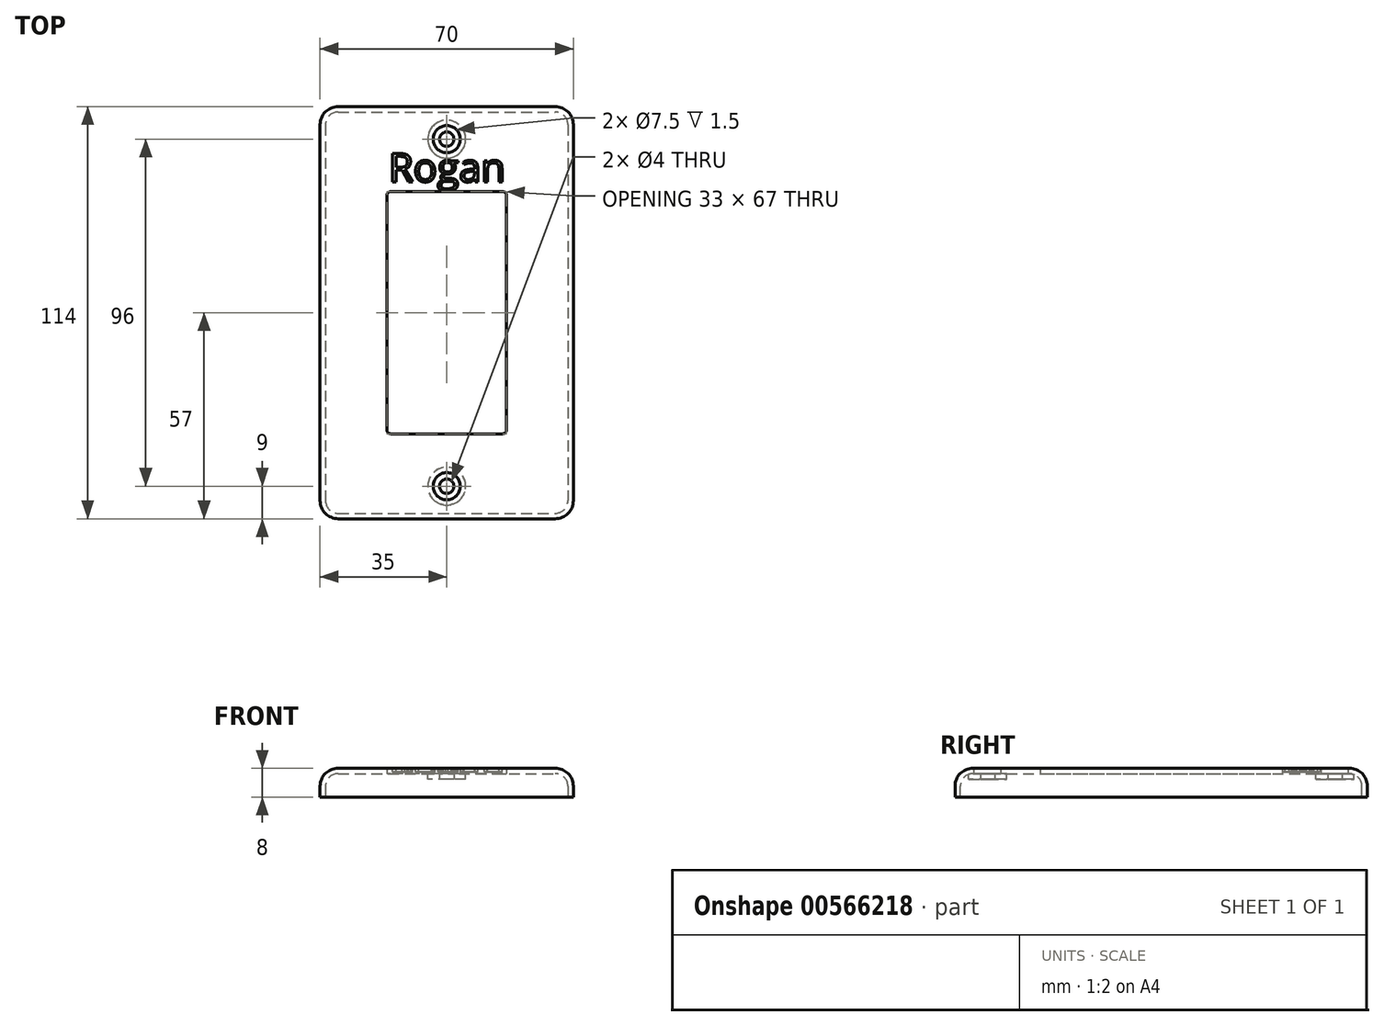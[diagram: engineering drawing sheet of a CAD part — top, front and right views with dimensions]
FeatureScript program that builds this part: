
annotation { "Feature Type Name" : "Feature", "Feature Type Description" : "" }
export const myFeature = defineFeature(function(context is Context, id is Id, definition is map)
    precondition{}
    {
        {
            var Q0;
            Q0=qCreatedBy(makeId("Top.planeOp"),FACE);
            var sketch = newSketch(context, id + "F0", { "sketchPlane" : qUnion([Q0])});
            skLineSegment(sketch, "E0.bottom", {"start": v(-35, 57) * mm, "end": v(35, 57) * mm});
            skLineSegment(sketch, "E0.top", {"start": v(-35, -57) * mm, "end": v(35, -57) * mm});
            skLineSegment(sketch, "E0.left", {"start": v(-35, 57) * mm, "end": v(-35, -57) * mm});
            skLineSegment(sketch, "E0.right", {"start": v(35, 57) * mm, "end": v(35, -57) * mm});
            skLineSegment(sketch, "E1.bottom", {"start": v(-16.5, 33.5) * mm, "end": v(16.5, 33.5) * mm});
            skLineSegment(sketch, "E1.top", {"start": v(-16.5, -33.5) * mm, "end": v(16.5, -33.5) * mm});
            skLineSegment(sketch, "E1.left", {"start": v(-16.5, 33.5) * mm, "end": v(-16.5, -33.5) * mm});
            skLineSegment(sketch, "E1.right", {"start": v(16.5, 33.5) * mm, "end": v(16.5, -33.5) * mm});
            skCircle(sketch, "E2", {"center": v(0, 48) * mm, "radius": 3.75 * mm});
            skCircle(sketch, "E3", {"center": v(0, -48) * mm, "radius": 3.75 * mm});
            skCircle(sketch, "E4", {"center": v(0, 48) * mm, "radius": 2 * mm});
            skCircle(sketch, "E5", {"center": v(0, -48) * mm, "radius": 2 * mm});
            skSolve(sketch);
        }
        {
            var Q0;
            Q0 = qSketchRegion(id + "F0", true);
            var Q1;
            Q1=makeQuery(id+"F0.imprint","IMPRINT",FACE,{"disambiguationData":[TD([[makeQuery(id+"F0.imprint","IMPRINT",EDGE,{"derivedFrom":sQuery(id+"F0.wireOp",EDGE,"E4")}),1.0]])]});
            var Q2;
            Q2=makeQuery(id+"F0.imprint","IMPRINT",FACE,{"disambiguationData":[TD([[makeQuery(id+"F0.imprint","IMPRINT",EDGE,{"derivedFrom":sQuery(id+"F0.wireOp",EDGE,"E2")}),1.0]])]});
            var Q3;
            Q3=makeQuery(id+"F0.imprint","IMPRINT",FACE,{"disambiguationData":[TD([[makeQuery(id+"F0.imprint","IMPRINT",EDGE,{"derivedFrom":sQuery(id+"F0.wireOp",EDGE,"E3")}),1.0]])]});
            var Q4;
            Q4=makeQuery(id+"F0.imprint","IMPRINT",FACE,{"disambiguationData":[TD([[makeQuery(id+"F0.imprint","IMPRINT",EDGE,{"derivedFrom":sQuery(id+"F0.wireOp",EDGE,"E5")}),1.0]])]});
            var Q5;
            Q5=makeQuery(id+"F0.imprint","IMPRINT",FACE,{"disambiguationData":[TD([[makeQuery(id+"F0.imprint","IMPRINT",EDGE,{"derivedFrom":sQuery(id+"F0.wireOp",EDGE,"E1.bottom")}),-1.0]])]});
            extrude(context, id + "F1", {"entities" : qUnion([Q0, Q1, Q2, Q3, Q4, Q5]), "depth" : 8 * mm, "offsetDistance" : 25 * mm});
        }
        {
            var Q0;
            Q0=makeQuery(id+"F1.opExtrude","CAP_EDGE",EDGE,{"disambiguationData":[OSD([sQuery(id+"F0.wireOp",EDGE,"E0.left")])],"isStart":false});
            var Q1;
            Q1=makeQuery(id+"F1.opExtrude","CAP_EDGE",EDGE,{"disambiguationData":[OSD([sQuery(id+"F0.wireOp",EDGE,"E0.bottom")])],"isStart":false});
            var Q2;
            Q2=makeQuery(id+"F1.opExtrude","CAP_EDGE",EDGE,{"disambiguationData":[OSD([sQuery(id+"F0.wireOp",EDGE,"E0.right")])],"isStart":false});
            var Q3;
            Q3=makeQuery(id+"F1.opExtrude","CAP_EDGE",EDGE,{"disambiguationData":[OSD([sQuery(id+"F0.wireOp",EDGE,"E0.top")])],"isStart":false});
            fillet(context, id + "F2", {"entities" : qUnion([Q0, Q1, Q2, Q3]), "radius" : 5 * mm, "tangentPropagation" : true, "allowEdgeOverflow" : false});
        }
        {
            var Q0;
            Q0=makeQuery(id+"F2.opFillet","BLEND_EDGE",EDGE,{"blendedFrom":[makeQuery(id+"F1.opExtrude","CAP_EDGE",EDGE,{"disambiguationData":[OSD([sQuery(id+"F0.wireOp",EDGE,"E0.bottom")])],"isStart":false}),makeQuery(id+"F1.opExtrude","CAP_EDGE",EDGE,{"disambiguationData":[OSD([sQuery(id+"F0.wireOp",EDGE,"E0.left")])],"isStart":false})],"blendedInto":[]});
            var Q1;
            Q1=makeQuery(id+"F2.opFillet","BLEND_EDGE",EDGE,{"blendedFrom":[makeQuery(id+"F1.opExtrude","CAP_EDGE",EDGE,{"disambiguationData":[OSD([sQuery(id+"F0.wireOp",EDGE,"E0.bottom")])],"isStart":false}),makeQuery(id+"F1.opExtrude","CAP_EDGE",EDGE,{"disambiguationData":[OSD([sQuery(id+"F0.wireOp",EDGE,"E0.right")])],"isStart":false})],"blendedInto":[]});
            var Q2;
            Q2=makeQuery(id+"F2.opFillet","BLEND_EDGE",EDGE,{"blendedFrom":[makeQuery(id+"F1.opExtrude","CAP_EDGE",EDGE,{"disambiguationData":[OSD([sQuery(id+"F0.wireOp",EDGE,"E0.top")])],"isStart":false}),makeQuery(id+"F1.opExtrude","CAP_EDGE",EDGE,{"disambiguationData":[OSD([sQuery(id+"F0.wireOp",EDGE,"E0.right")])],"isStart":false})],"blendedInto":[]});
            var Q3;
            Q3=makeQuery(id+"F2.opFillet","BLEND_EDGE",EDGE,{"blendedFrom":[makeQuery(id+"F1.opExtrude","CAP_EDGE",EDGE,{"disambiguationData":[OSD([sQuery(id+"F0.wireOp",EDGE,"E0.top")])],"isStart":false}),makeQuery(id+"F1.opExtrude","CAP_EDGE",EDGE,{"disambiguationData":[OSD([sQuery(id+"F0.wireOp",EDGE,"E0.left")])],"isStart":false})],"blendedInto":[]});
            fillet(context, id + "F3", {"entities" : qUnion([Q0, Q1, Q2, Q3]), "radius" : 5 * mm, "tangentPropagation" : true, "allowEdgeOverflow" : false});
        }
        {
            var Q0;
            Q0=makeQuery(id+"F1.opExtrude","CAP_FACE",FACE,{"disambiguationData":[OSD([sQuery(id+"F0.wireOp",EDGE,"E0.bottom"),sQuery(id+"F0.wireOp",EDGE,"E0.top"),sQuery(id+"F0.wireOp",EDGE,"E0.left"),sQuery(id+"F0.wireOp",EDGE,"E0.right"),sQuery(id+"F0.wireOp",EDGE,"E1.bottom"),sQuery(id+"F0.wireOp",EDGE,"E1.top"),sQuery(id+"F0.wireOp",EDGE,"E1.left"),sQuery(id+"F0.wireOp",EDGE,"E1.right"),sQuery(id+"F0.wireOp",EDGE,"E2"),sQuery(id+"F0.wireOp",EDGE,"E3")])],"isStart":false});
            var sketch = newSketch(context, id + "F4", { "sketchPlane" : qUnion([Q0])});
            skText(sketch, "E6", { "text": "Rogan", "fontName": "OpenSans-Regular.ttf"});
            const initialGuessF4  = {"E6": [-0.016, 0.0362, 1, 0, 0.00788]};
            skSetInitialGuess(sketch, initialGuessF4);
            skSolve(sketch);
        }
        {
            var Q0;
            {var subQ0=sQuery(id+"F0.wireOp",EDGE,"E1.right");var subQ1=sQuery(id+"F0.wireOp",EDGE,"E1.top");var subQ2=sQuery(id+"F0.wireOp",EDGE,"E1.left");var subQ3=sQuery(id+"F0.wireOp",EDGE,"E1.bottom");var subQ4=sQuery(id+"F0.wireOp",EDGE,"E0.right");var subQ5=sQuery(id+"F0.wireOp",EDGE,"E0.top");var subQ6=sQuery(id+"F0.wireOp",EDGE,"E0.left");var subQ7=sQuery(id+"F0.wireOp",EDGE,"E0.bottom");Q0=makeQuery(id+"F8.boolean.opBoolean","SPLIT",FACE,{"disambiguationData":[TD([makeQuery(id+"F1.opExtrude","SWEPT_FACE",FACE,{"disambiguationData":[OSD([subQ3])]})])],"derivedFrom":makeQuery(id+"F1.opExtrude","CAP_FACE",FACE,{"disambiguationData":[OSD([subQ7,subQ5,subQ6,subQ4,subQ3,subQ1,subQ2,subQ0])],"isStart":false})});}
            var sketch = newSketch(context, id + "F5", { "sketchPlane" : qUnion([Q0])});
            skCircle(sketch, "E7.0", {"center": v(0, 48) * mm, "radius": 3.75 * mm});
            skCircle(sketch, "E8.0", {"center": v(0, -48) * mm, "radius": 3.75 * mm});
            skSolve(sketch);
        }
        {
            var Q0;
            Q0 = qSketchRegion(id + "F5", true);
            extrude(context, id + "F6", {"entities" : qUnion([Q0]), "operationType" : NewBodyOperationType.REMOVE, "oppositeDirection" : true, "depth" : 1.5 * mm, "offsetDistance" : 25 * mm});
        }
        {
            var Q0;
            {var subQ0=sQuery(id+"F0.wireOp",EDGE,"E3");var subQ1=sQuery(id+"F0.wireOp",EDGE,"E2");Q0=makeQuery(id+"FkINO1WwK0jsU7R_1.boolean.opBoolean","MERGE",FACE,{"derivedFrom":[makeQuery(id+"F1.opExtrude","CAP_FACE",FACE,{"disambiguationData":[OSD([sQuery(id+"F0.wireOp",EDGE,"E0.bottom"),sQuery(id+"F0.wireOp",EDGE,"E0.top"),sQuery(id+"F0.wireOp",EDGE,"E0.left"),sQuery(id+"F0.wireOp",EDGE,"E0.right"),sQuery(id+"F0.wireOp",EDGE,"E1.bottom"),sQuery(id+"F0.wireOp",EDGE,"E1.top"),sQuery(id+"F0.wireOp",EDGE,"E1.left"),sQuery(id+"F0.wireOp",EDGE,"E1.right"),subQ1,subQ0])],"isStart":true}),makeQuery(id+"FkINO1WwK0jsU7R_1.opExtrude","CAP_FACE",FACE,{"disambiguationData":[OSD([subQ1,sQuery(id+"F0.wireOp",EDGE,"E4")])],"isStart":true}),makeQuery(id+"FkINO1WwK0jsU7R_1.opExtrude","CAP_FACE",FACE,{"disambiguationData":[OSD([subQ0,sQuery(id+"F0.wireOp",EDGE,"E5")])],"isStart":true})]});}
            shell(context, id + "F7", {"entities" : qUnion([Q0]), "thickness" : 1.5 * mm});
        }
        {
            var Q0;
            Q0 = qSketchRegion(id + "F4", true);
            extrude(context, id + "F8", {"entities" : qUnion([Q0]), "operationType" : NewBodyOperationType.REMOVE, "oppositeDirection" : true, "depth" : 1 * mm, "offsetDistance" : 25 * mm});
        }
        {
            var Q0;
            Q0=makeQuery(id+"F0.imprint","IMPRINT",FACE,{"disambiguationData":[TD([[makeQuery(id+"F0.imprint","IMPRINT",EDGE,{"derivedFrom":sQuery(id+"F0.wireOp",EDGE,"E4")}),1.0]])]});
            var Q1;
            Q1=makeQuery(id+"F0.imprint","IMPRINT",FACE,{"disambiguationData":[TD([[makeQuery(id+"F0.imprint","IMPRINT",EDGE,{"derivedFrom":sQuery(id+"F0.wireOp",EDGE,"E5")}),1.0]])]});
            var Q2;
            Q2=makeQuery(id+"F0.imprint","IMPRINT",FACE,{"disambiguationData":[TD([[makeQuery(id+"F0.imprint","IMPRINT",EDGE,{"derivedFrom":sQuery(id+"F0.wireOp",EDGE,"E1.bottom")}),-1.0]])]});
            extrude(context, id + "F9", {"entities" : qUnion([Q0, Q1, Q2]), "operationType" : NewBodyOperationType.REMOVE, "endBound" : BoundingType.THROUGH_ALL, "depth" : 25 * mm, "offsetDistance" : 25 * mm});
        }
        {
            var Q0;
            Q0=makeQuery(id+"F9.boolean.opBoolean","COPY",EDGE,{"derivedFrom":makeQuery(id+"F9.opExtrude","SWEPT_EDGE",EDGE,{"disambiguationData":[OSD([sQuery(id+"F0.wireOp",EDGE,"E1.bottom"),sQuery(id+"F0.wireOp",EDGE,"E1.right")])]})});
            var Q1;
            Q1=makeQuery(id+"F9.boolean.opBoolean","COPY",EDGE,{"derivedFrom":makeQuery(id+"F9.opExtrude","SWEPT_EDGE",EDGE,{"disambiguationData":[OSD([sQuery(id+"F0.wireOp",EDGE,"E1.top"),sQuery(id+"F0.wireOp",EDGE,"E1.right")])]})});
            var Q2;
            Q2=makeQuery(id+"F9.boolean.opBoolean","COPY",EDGE,{"derivedFrom":makeQuery(id+"F9.opExtrude","SWEPT_EDGE",EDGE,{"disambiguationData":[OSD([sQuery(id+"F0.wireOp",EDGE,"E1.bottom"),sQuery(id+"F0.wireOp",EDGE,"E1.left")])]})});
            var Q3;
            Q3=makeQuery(id+"F9.boolean.opBoolean","COPY",EDGE,{"derivedFrom":makeQuery(id+"F9.opExtrude","SWEPT_EDGE",EDGE,{"disambiguationData":[OSD([sQuery(id+"F0.wireOp",EDGE,"E1.top"),sQuery(id+"F0.wireOp",EDGE,"E1.left")])]})});
            fillet(context, id + "F10", {"entities" : qUnion([Q0, Q1, Q2, Q3]), "radius" : 1 * mm, "tangentPropagation" : true, "allowEdgeOverflow" : false});
        }
    });
